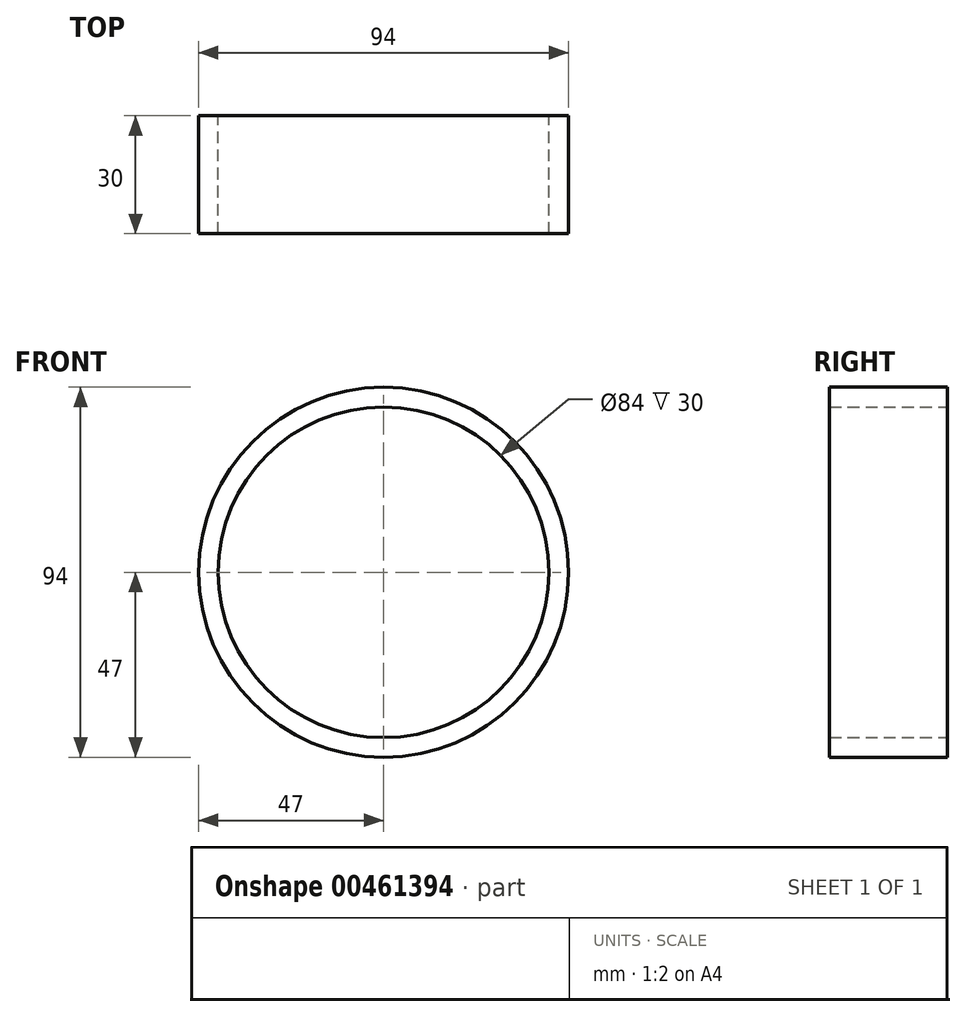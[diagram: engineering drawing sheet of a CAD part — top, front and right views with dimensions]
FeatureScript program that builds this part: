
annotation { "Feature Type Name" : "Feature", "Feature Type Description" : "" }
export const myFeature = defineFeature(function(context is Context, id is Id, definition is map)
    precondition{}
    {
        {
            var Q0;
            Q0=qCreatedBy(makeId("Front.planeOp"),FACE);
            var sketch = newSketch(context, id + "F0", { "sketchPlane" : qUnion([Q0])});
            skCircle(sketch, "E0", {"center": v(0, 0) * mm, "radius": 42 * mm});
            skCircle(sketch, "E1", {"center": v(0, 0) * mm, "radius": 47 * mm});
            skSolve(sketch);
        }
        {
            var Q0;
            Q0 = qSketchRegion(id + "F0", true);
            extrude(context, id + "F1", {"entities" : qUnion([Q0]), "depth" : 30 * mm});
        }
    });
